# Revit family: EVU-2082
name_source: partatom
category: Communication Devices
revit_build: Autodesk Revit 2017 (Build: 20160225_1515(x64)
units: mm (PartAtom-declared; Revit-internal decimal feet)

## family parameters
Always vertical = Yes
Cut with Voids When Loaded = No
Maintain Annotation Orientation = Yes
OmniClass Number = 23.85.10.11.11.21
OmniClass Title = Speakers
Part Type = Normal
Room Calculation Point = No
Round Connector Dimension = Use Diameter
Shared = No
Work Plane-Based = Yes

## types (2) — shared parameters
ArchitectsAndEngineersSpecs = https://www.electrovoice.com
BackHeight = 134.42 mm  [stored 0.44101 ft]
Depth = 237.21 mm  [stored 0.778248 ft]
Description = 1.3" (33mm) diaphgram, 1.4" (36mm) exit pure titanium compression driver. 8" (203mm) LF transducer. Advanced third-order crossover network with HF protection. Coverage pattern: 90° x 50° Constant Directivity rotatable waveguide. 92 dB sensitivity, 120 dB maximum SPL. System raiting: 175 W continuous, 700 W peak. Universal U-bracket included.
Disclaimer = http://resource.boschsecurity.com
FrontHeight = 247.23 mm  [stored 0.811122 ft]
IfcExportAs = IfcBuildingElementProxy
IfcExportType = IfcBuildingElementProxyType
InstallationManual = https://www.electrovoice.com
Length = 615.47 mm  [stored 2.01926 ft]
Manufacturer = Electro Voice
ManufacturerURL = https://www.electrovoice.com
PlanningTools = http://www.electrovoice.com
ProductInformation = https://www.electrovoice.com
Uniclass2015Code = Pr_60_75_08_02
Version = 1
zero-valued in all types: Default Elevation

## per-type parameters (varying)
| type | CTN | GrillMaterial | LoudspeakerMaterial | MaterialRALColour | ModelNumber |
| EVU2082/95Wht_Single_8_Inch_Two_Way_White | EVU2082/95WHT | 16GA Powder-coatedGalvanneal - W | 13-plyWeather-resistantBirchEVCoat -RAL9010 | RAL9010 | F.01U.216.256 |
| EVU2082/95BLK_Single_8_Inch_Two_Way_Black | EVU2082/95BLK | 16GA Powder-coatedGalvanneal - B | 13-plyWeather-resistantBirchEVCoat -RAL9004 | RAL9004 | F.01U.216.255 |

note: [stored X ft] marks values corroborated as IEEE doubles in the binary element streams (Revit-internal decimal feet)

## geometry (parser evidence)
native form markers: Sweep x6
no freeform markers — native parametric forms only
